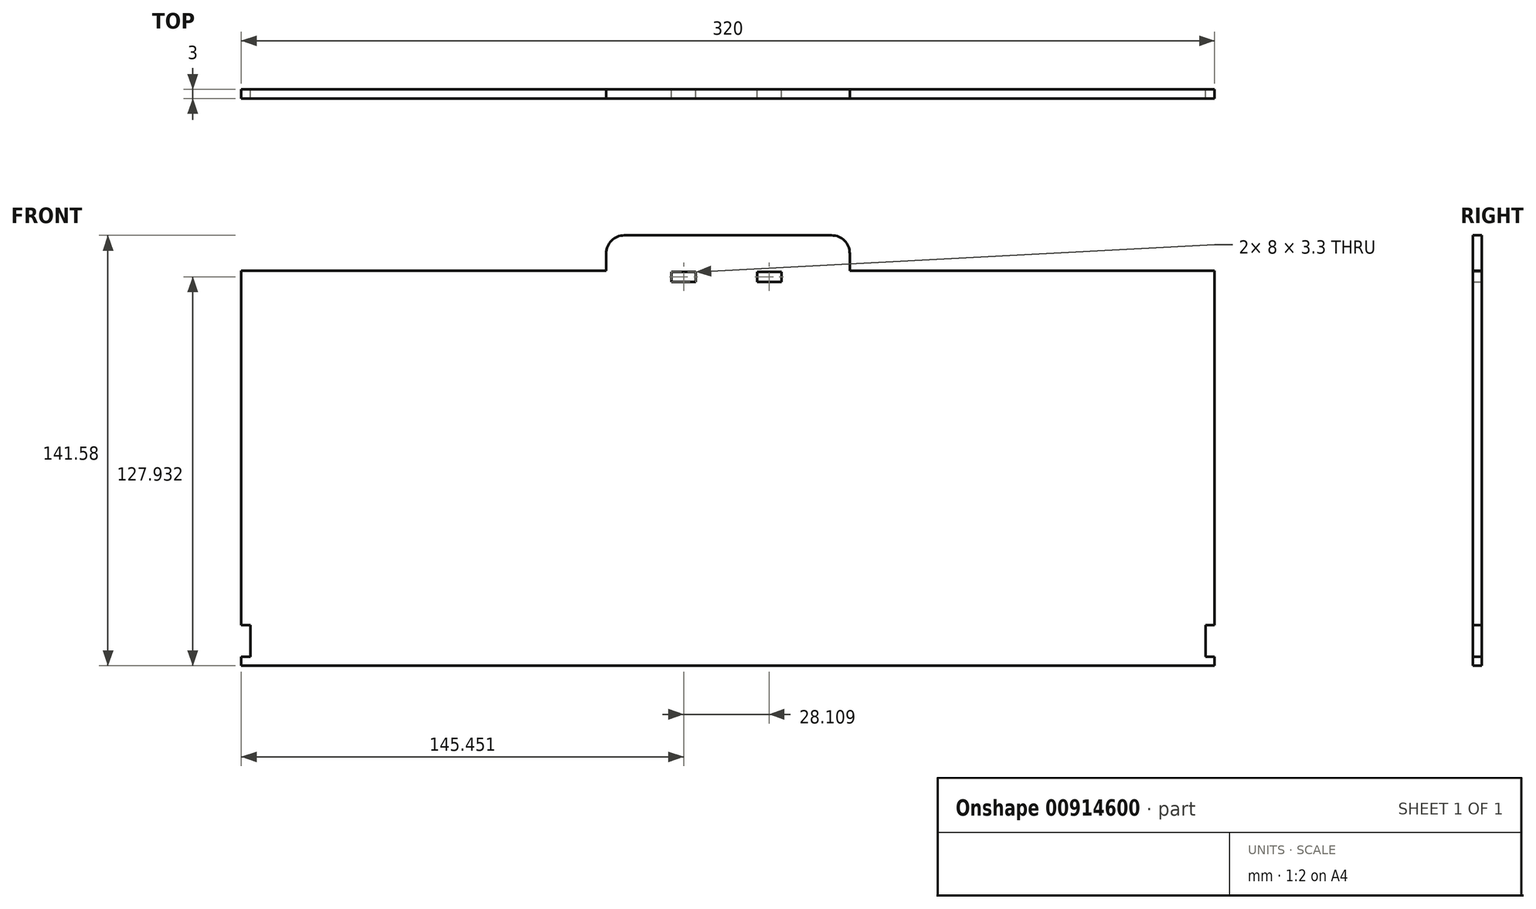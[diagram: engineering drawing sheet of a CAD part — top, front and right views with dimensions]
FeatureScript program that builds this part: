
annotation { "Feature Type Name" : "Feature", "Feature Type Description" : "" }
export const myFeature = defineFeature(function(context is Context, id is Id, definition is map)
    precondition{}
    {
        {
            var Q0;
            Q0=qCreatedBy(makeId("Front.planeOp"),FACE);
            var sketch = newSketch(context, id + "F0", { "sketchPlane" : qUnion([Q0])});
            skLineSegment(sketch, "E0", {"start": v(-220, -38.78) * mm, "end": v(100, -38.78) * mm});
            skLineSegment(sketch, "E1", {"start": v(97, -35.78) * mm, "end": v(100, -35.78) * mm});
            skLineSegment(sketch, "E2", {"start": v(100, -35.78) * mm, "end": v(100, -38.78) * mm});
            skLineSegment(sketch, "E3", {"start": v(97, -35.78) * mm, "end": v(97, -25.44) * mm});
            skLineSegment(sketch, "E4", {"start": v(100, -25.44) * mm, "end": v(100, 91.22) * mm});
            skLineSegment(sketch, "E5", {"start": v(-220, -38.78) * mm, "end": v(-220, -35.78) * mm});
            skLineSegment(sketch, "E6", {"start": v(-220, -35.78) * mm, "end": v(-217, -35.78) * mm});
            skLineSegment(sketch, "E7", {"start": v(-217, -35.78) * mm, "end": v(-217, -25.44) * mm});
            skLineSegment(sketch, "E8", {"start": v(-217, -25.44) * mm, "end": v(-220, -25.44) * mm});
            skLineSegment(sketch, "E9", {"start": v(-220, -25.44) * mm, "end": v(-220, 91.22) * mm});
            skLineSegment(sketch, "E10", {"start": v(97, -25.44) * mm, "end": v(100, -25.44) * mm});
            skLineSegment(sketch, "E11", {"start": v(-220, 91.22) * mm, "end": v(-100.05, 91.22) * mm});
            skLineSegment(sketch, "E12.top", {"start": v(-25.95, 102.8) * mm, "end": v(-94.05, 102.8) * mm});
            skLineSegment(sketch, "E12.left", {"start": v(-19.95, 90.8) * mm, "end": v(-19.95, 96.8) * mm});
            skLineSegment(sketch, "E12.right", {"start": v(-100.05, 90.8) * mm, "end": v(-100.05, 96.8) * mm});
            skPoint(sketch, "E13.visualSharp", {"position": v(-19.95, 102.8) * mm});
            skArc(sketch, "E13.filletArc", {"start": v(-19.95, 96.8) * mm, "mid": v(-21.7, 101.04) * mm, "end": v(-25.95, 102.8) * mm});
            skPoint(sketch, "E14.visualSharp", {"position": v(-100.05, 102.8) * mm});
            skArc(sketch, "E14.filletArc", {"start": v(-94.05, 102.8) * mm, "mid": v(-98.3, 101.04) * mm, "end": v(-100.05, 96.8) * mm});
            skLineSegment(sketch, "E15", {"start": v(-20.44, 90.8) * mm, "end": v(-20.5, 90.8) * mm});
            skLineSegment(sketch, "E16.bottom", {"start": v(-42.44, 90.8) * mm, "end": v(-50.44, 90.8) * mm});
            skLineSegment(sketch, "E16.top", {"start": v(-42.44, 87.5) * mm, "end": v(-50.44, 87.5) * mm});
            skLineSegment(sketch, "E16.left", {"start": v(-42.44, 90.8) * mm, "end": v(-42.44, 87.5) * mm});
            skLineSegment(sketch, "E16.right", {"start": v(-50.44, 90.8) * mm, "end": v(-50.44, 87.5) * mm});
            skLineSegment(sketch, "E17.MirrorCS", {"start": v(-78.55, 90.8) * mm, "end": v(-70.55, 90.8) * mm});
            skLineSegment(sketch, "E18.MirrorCS", {"start": v(-70.55, 90.8) * mm, "end": v(-70.55, 87.5) * mm});
            skLineSegment(sketch, "E19.MirrorCS", {"start": v(-100.55, 90.8) * mm, "end": v(-100.05, 90.8) * mm});
            skLineSegment(sketch, "E20.MirrorCS", {"start": v(-78.55, 87.5) * mm, "end": v(-70.55, 87.5) * mm});
            skLineSegment(sketch, "E21.MirrorCS", {"start": v(-78.55, 90.8) * mm, "end": v(-78.55, 87.5) * mm});
            skLineSegment(sketch, "E22.trimOffspring", {"start": v(-50.44, 90.8) * mm, "end": v(-42.44, 90.8) * mm});
            skLineSegment(sketch, "E23.trimOffspring", {"start": v(-70.55, 90.8) * mm, "end": v(-78.55, 90.8) * mm});
            skLineSegment(sketch, "E24.trimOffspring", {"start": v(-19.95, 91.22) * mm, "end": v(100, 91.22) * mm});
            skLineSegment(sketch, "E25", {"start": v(-100.05, 91.22) * mm, "end": v(-19.95, 91.22) * mm, "construction": true});
            skPoint(sketch, "E26", {"position": v(-60, 91.22) * mm});
            skSolve(sketch);
        }
        {
            var Q0;
            Q0=makeQuery(id+"F0.imprint","IMPRINT",FACE,{"disambiguationData":[TD([[makeQuery(id+"F0.imprint","IMPRINT",EDGE,{"derivedFrom":sQuery(id+"F0.wireOp",EDGE,"E0")}),1.0]])]});
            extrude(context, id + "F1", {"entities" : qUnion([Q0]), "depth" : 3 * mm, "offsetDistance" : 25 * mm});
        }
    });
